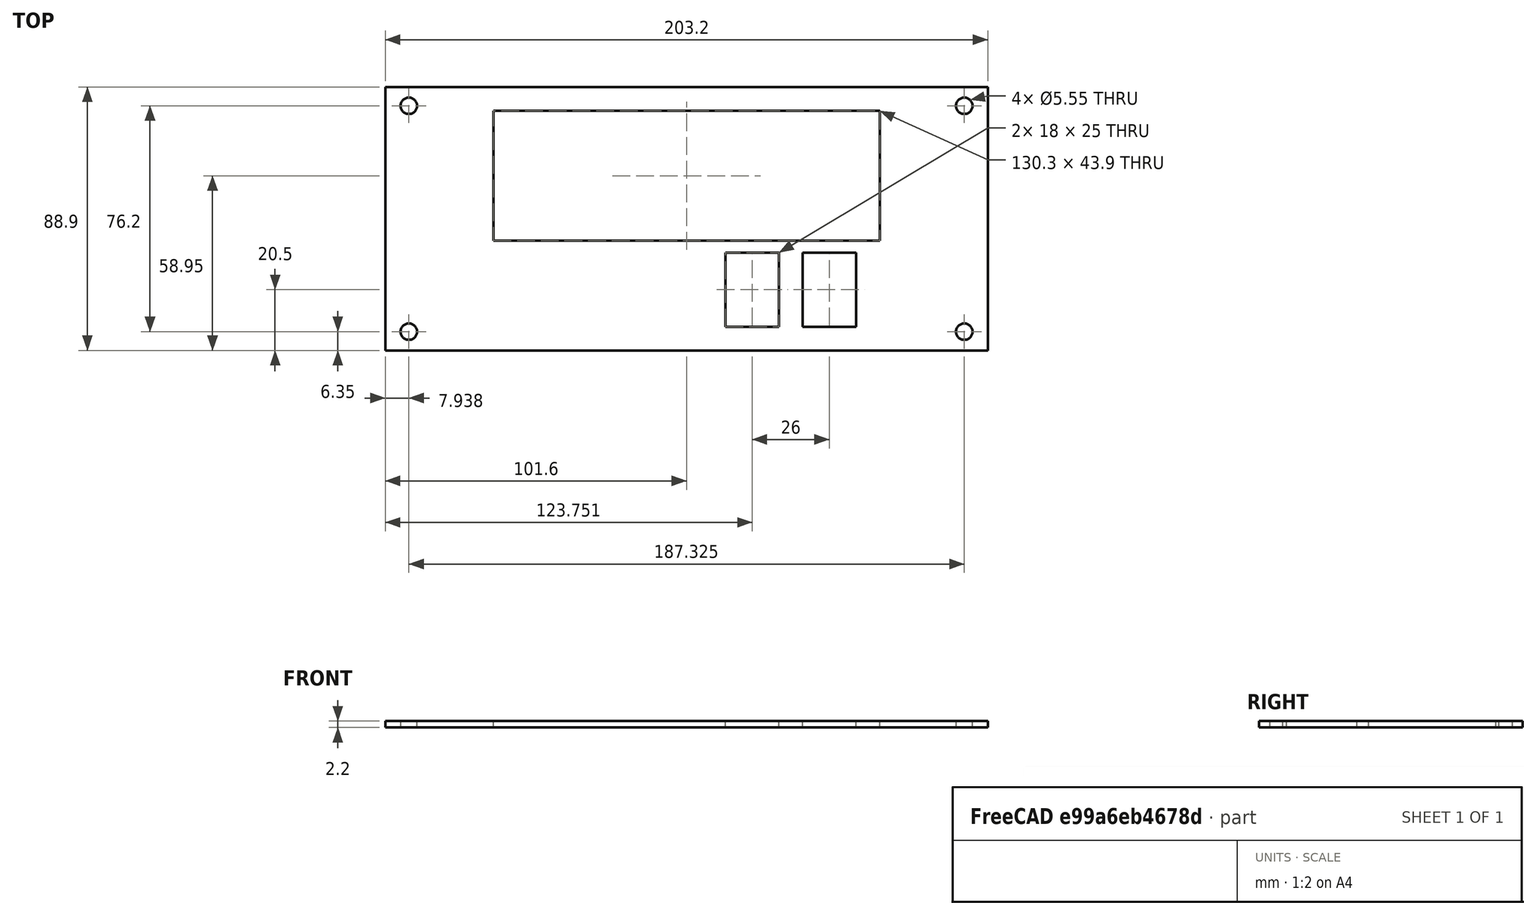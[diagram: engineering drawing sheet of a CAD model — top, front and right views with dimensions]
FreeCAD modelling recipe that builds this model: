
FCSTD DOCUMENT  (FreeCAD 0.19R24366 (Git))
Label: 1U_Modem_v0
License: All rights reserved
LicenseURL: http://en.wikipedia.org/wiki/All_rights_reserved
objects: Sketcher::SketchObject×1, PartDesign::Pad×1, PartDesign::Body×1
note: 4 computed .brp shape members not serialized (recipe doc carries the construction recipe); baked Part::Feature solids carry a one-line shape summary decoded from their .brp

FEATURE [Sketcher::SketchObject] Sketch
  FullyConstrained = true
  MapMode = 5
  Support = -> [XY_Plane001]
  sketch-geometry (20):
    g0: LineSegment StartX=-101.6 StartY=44.45 StartZ=0 EndX=101.6 EndY=44.45 EndZ=0
    g1: LineSegment StartX=101.6 StartY=44.45 StartZ=0 EndX=101.6 EndY=-44.45 EndZ=0
    g2: LineSegment StartX=101.6 StartY=-44.45 StartZ=0 EndX=-101.6 EndY=-44.45 EndZ=0
    g3: LineSegment StartX=-101.6 StartY=-44.45 StartZ=0 EndX=-101.6 EndY=44.45 EndZ=0
    g4: Circle CenterX=-93.6625 CenterY=38.1 CenterZ=0 NormalX=0 NormalY=0 NormalZ=1 AngleXU=0 Radius=2.775
    g5: Circle CenterX=-93.6625 CenterY=-38.1 CenterZ=0 NormalX=0 NormalY=0 NormalZ=1 AngleXU=0 Radius=2.775
    g6: Circle CenterX=93.6625 CenterY=38.1 CenterZ=0 NormalX=0 NormalY=0 NormalZ=1 AngleXU=0 Radius=2.775
    g7: Circle CenterX=93.6625 CenterY=-38.1 CenterZ=0 NormalX=0 NormalY=0 NormalZ=1 AngleXU=0 Radius=2.775
    g8: LineSegment StartX=-65.151 StartY=36.45 StartZ=0 EndX=65.151 EndY=36.45 EndZ=0
    g9: LineSegment StartX=65.151 StartY=36.45 StartZ=0 EndX=65.151 EndY=-7.45 EndZ=0
    g10: LineSegment StartX=65.151 StartY=-7.45 StartZ=0 EndX=-65.151 EndY=-7.45 EndZ=0
    g11: LineSegment StartX=-65.151 StartY=-7.45 StartZ=0 EndX=-65.151 EndY=36.45 EndZ=0
    g12: LineSegment StartX=39.151 StartY=-11.45 StartZ=0 EndX=57.151 EndY=-11.45 EndZ=0
    g13: LineSegment StartX=57.151 StartY=-11.45 StartZ=0 EndX=57.151 EndY=-36.45 EndZ=0
    g14: LineSegment StartX=57.151 StartY=-36.45 StartZ=0 EndX=39.151 EndY=-36.45 EndZ=0
    g15: LineSegment StartX=39.151 StartY=-36.45 StartZ=0 EndX=39.151 EndY=-11.45 EndZ=0
    g16: LineSegment StartX=13.151 StartY=-11.45 StartZ=0 EndX=31.151 EndY=-11.45 EndZ=0
    g17: LineSegment StartX=31.151 StartY=-11.45 StartZ=0 EndX=31.151 EndY=-36.45 EndZ=0
    g18: LineSegment StartX=31.151 StartY=-36.45 StartZ=0 EndX=13.151 EndY=-36.45 EndZ=0
    g19: LineSegment StartX=13.151 StartY=-36.45 StartZ=0 EndX=13.151 EndY=-11.45 EndZ=0
  constraints (55):
    c: Coincident(g0,g1)
    c: Coincident(g1,g2)
    c: Coincident(g2,g3)
    c: Coincident(g3,g0)
    c: Horizontal(g0)
    c: Horizontal(g2)
    c: Vertical(g1)
    c: Vertical(g3)
    c: DistanceX(g0,g0) = 203.2
    c: DistanceY(g3,g3) = 88.9
    c: Symmetric(g0,g2,g-1)
    c: Diameter(g4) = 5.55
    c: DistanceX(g0,g4) = 7.9375
    c: DistanceY(g4,g0) = 6.35
    c: Diameter(g5) = 5.55
    c: Symmetric(g4,g5,g-1)
    c: Diameter(g6) = 5.55
    c: Diameter(g7) = 5.55
    c: Symmetric(g6,g4,g-2)
    c: Symmetric(g7,g5,g-2)
    c: Coincident(g8,g9)
    c: Coincident(g9,g10)
    c: Coincident(g10,g11)
    c: Coincident(g11,g8)
    c: Horizontal(g10)
    c: Vertical(g9)
    c: Vertical(g11)
    c: DistanceX(g8,g8) = 130.302
    c: DistanceY(g11,g11) = 43.9
    c: Symmetric(g8,g8,g-2)
    c: DistanceY(g8,g0) = 8
    c: Coincident(g12,g13)
    c: Coincident(g13,g14)
    c: Coincident(g14,g15)
    c: Coincident(g15,g12)
    c: Horizontal(g12)
    c: Horizontal(g14)
    c: Vertical(g13)
    c: Vertical(g15)
    c: DistanceX(g12,g12) = 18
    c: DistanceY(g13,g13) = 25
    c: DistanceY(g1,g13) = 8
    c: Coincident(g16,g17)
    c: Coincident(g17,g18)
    c: Coincident(g18,g19)
    c: Coincident(g19,g16)
    c: Horizontal(g16)
    c: Horizontal(g18)
    c: Vertical(g17)
    c: Vertical(g19)
    c: DistanceX(g16,g16) = 18
    c: DistanceY(g19,g19) = 25
    c: DistanceY(g1,g17) = 8
    c: DistanceX(g12,g9) = 8
    c: DistanceX(g16,g12) = 8
FEATURE [PartDesign::Pad] Pad
  Direction = (1,1,1)
  Length = 2.2
  Length2 = 100
  Profile = -> Sketch
  Refine = true
  Type = 0
FEATURE [PartDesign::Body] Body001
  Group = -> [Sketch,Pad]
  Origin = -> Origin001
  Tip = -> Pad
